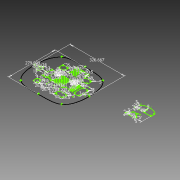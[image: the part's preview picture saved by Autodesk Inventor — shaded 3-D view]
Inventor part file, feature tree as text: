
AUTODESK INVENTOR PART (.ipt)
format: ipt  version: 2012 (Build 160160000, 160)  size: 227,328 bytes
history: native  units: mm
features: sketch x1
ambient origin geometry x8: Origin, YZ Plane, XZ Plane, XY Plane, X Axis, Y Axis, Z Axis, Center Point
feature tree (1):
  sketch  "Sketch1"  dims[d51=3.0mm d54=3.0mm d64=3.0mm d69=3.0mm d76=3.0mm d77=3.0mm d78=51.0mm d82=51.0mm d91=25.0mm d94=51.0mm d96=51.0mm d116=64.0mm d117=3.0mm d118=3.0mm d119=3.0mm d120=3.0mm d122=5.632993mm d125=4.7mm d126=5.0mm d128=10.0mm d129=5.0mm d131=5.0mm d132=66.0mm d134=3.0mm d135=3.0mm d137=3.0mm d138=5.682993mm d139=4.7mm d140=5.0mm d141=10.0mm d142=5.0mm d143=3.0mm d144=5.0mm d145=5.0mm d150=3.0mm d160=36.2mm d162=50.0mm d163=5.0mm d164=40.0mm d165=28.5mm d166=5.0mm d170=5.0mm d171=35.0mm d172=5.0mm d177=66.0mm d184=3.0mm d185=10.0mm d186=25.0mm d187=3.0mm d188=25.0mm d189=10.0mm d190=3.0mm d196=3.0mm d197=3.0mm d198=30.0mm d199=60.0mm d200=10.0mm d201=35.0mm d202=3.0mm d203=30.0mm d204=34.23504mm d205=34.23504mm d206=35.0mm d207=30.0mm d208=31.5mm d209=31.5mm d210=50.55mm d213=5.554212mm d215=5.0mm d216=5.554212mm d217=5.117007mm d219=5.0mm d220=5.0mm d221=5.117007mm d232=14.0mm d236=2.0mm d238=13.0mm d239=3.0mm d244=3.0mm d245=26.4mm d246=22.0mm d247=8.0mm d248=3.0mm d249=3.0mm d250=26.4mm d251=22.0mm d252=16.0mm d253=16.0mm d271=30.0mm d274=28.5mm d275=5.0mm d276=279.999493mm d277=326.667217mm d278=20.5mm d279=5.0mm d280=17.0mm d282=60.0mm d283=5.0mm d284=5.0mm d285=5.0mm d286=94.0mm d288=25.0mm d289=5.0mm d291=3.0mm d292=4.0mm d293=4.0mm d294=49.0mm d295=8.0mm d296=20.0mm d300=3.0mm d301=4.0mm d302=4.0mm d303=49.0mm d310=5.0mm d311=5.0mm]
